# Revit family: Equipment-Gym-Draper_Inc.-Forward_Folding_Backstop-TF-202
name_source: partatom
category: Specialty Equipment
revit_build: Autodesk Revit Architecture 2012 (Build: 20110309_2315(x64)
units: mm (PartAtom-declared; Revit-internal decimal feet)

## types (1)
- NOT A TYPE - LOAD TYPE CATALOG
    Apparent Load = 746 VA
    Backboard = Glass - Draper Inc. - Backboard Glass
    Backboard Frame = Metal - Draper Inc. - Aluminum
    Backboard Height = 4' - 0"
    Backboard Length = 6' - 0"
    C = 11 1/4"
    Constraint C = 11 1/4"
    Description = Basketball Backstop
    Fan Backstop = No
    Frame = Metal - Draper Inc. - White Paint
    Frequency = 60 Hz
    Manufacturer = Draper Inc.
    Model = TF-20
    Number of Poles = 1
    Power Factor = 1
    Product Documentation Link = http://www.draperinc.com
    Product Name = Forward Folding Basketball Backstops
    Product Page URL = http://www.draperinc.com
    Rect Backstop = Yes
    Stripe = Metal - Draper Inc. - White Paint
    URL = http://www.draperinc.com
    Voltage = 120 V

## geometry (parser evidence)
native form markers: Sweep x11
no freeform markers — native parametric forms only
